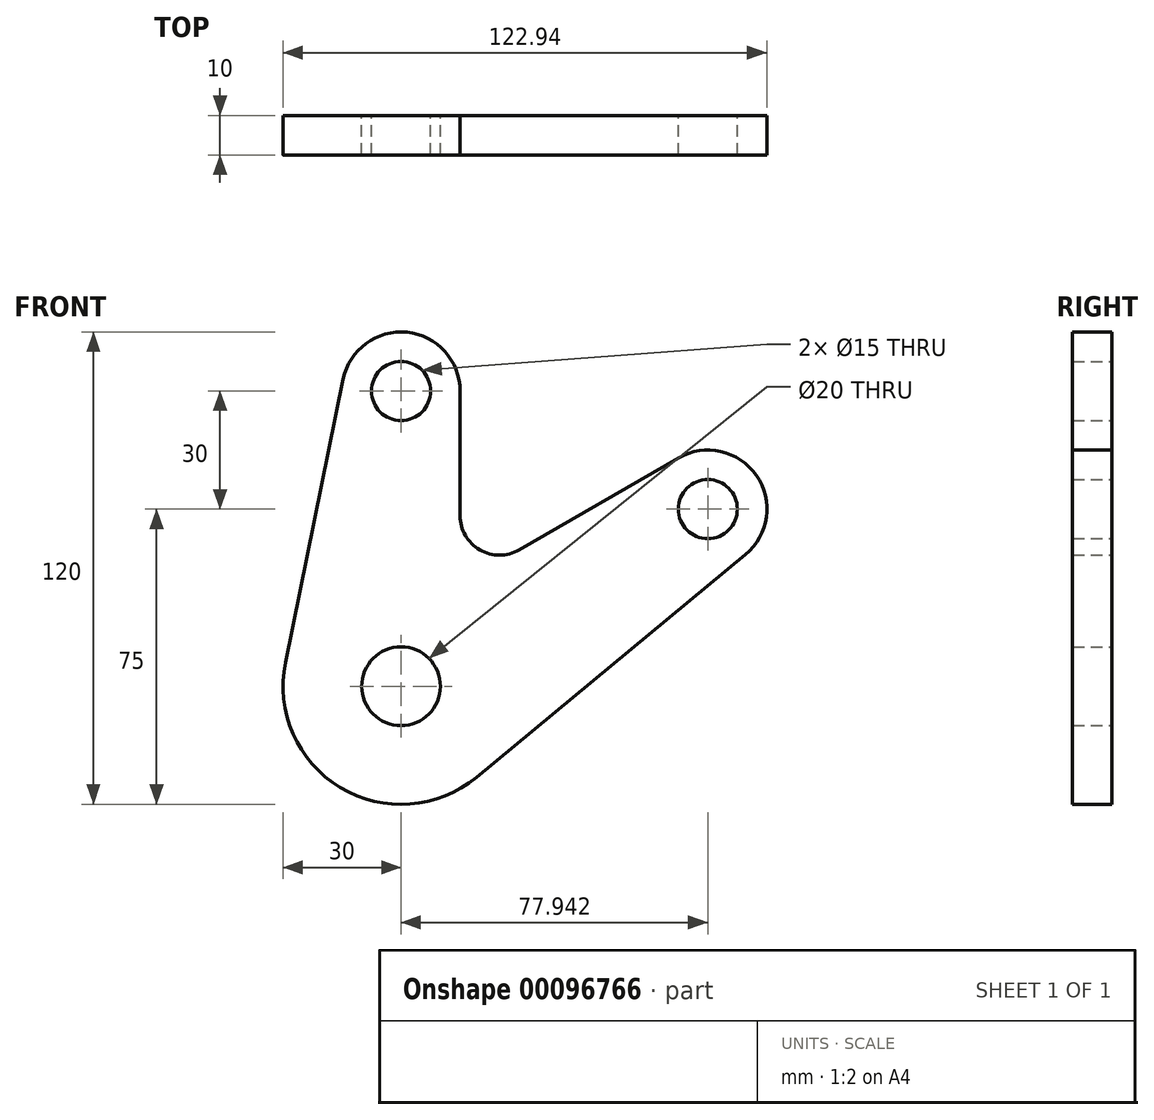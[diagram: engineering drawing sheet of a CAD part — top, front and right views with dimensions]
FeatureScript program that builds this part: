
annotation { "Feature Type Name" : "Feature", "Feature Type Description" : "" }
export const myFeature = defineFeature(function(context is Context, id is Id, definition is map)
    precondition{}
    {
        {
            var Q0;
            Q0=qCreatedBy(makeId("Front.planeOp"),FACE);
            var sketch = newSketch(context, id + "F0", { "sketchPlane" : qUnion([Q0])});
            skCircle(sketch, "E0", {"center": v(0, 0) * mm, "radius": 10 * mm});
            skCircle(sketch, "E1", {"center": v(0, 75) * mm, "radius": 7.5 * mm});
            skCircle(sketch, "E2", {"center": v(77.94, 45) * mm, "radius": 7.5 * mm});
            skLineSegment(sketch, "E3", {"start": v(0, 75) * mm, "end": v(0, 0) * mm, "construction": true});
            skLineSegment(sketch, "E4", {"start": v(0, 0) * mm, "end": v(77.94, 45) * mm, "construction": true});
            skArc(sketch, "E5", {"start": v(15, 75) * mm, "mid": v(1.5, 89.92) * mm, "end": v(-14.7, 78) * mm});
            skArc(sketch, "E6", {"start": v(87.5, 33.44) * mm, "mid": v(90.26, 53.56) * mm, "end": v(70.44, 58) * mm});
            skArc(sketch, "E7", {"start": v(-29.4, 6) * mm, "mid": v(-15.44, -25.72) * mm, "end": v(19.12, -23.12) * mm});
            skLineSegment(sketch, "E8", {"start": v(-14.7, 78) * mm, "end": v(-29.4, 6) * mm});
            skLineSegment(sketch, "E9", {"start": v(87.5, 33.44) * mm, "end": v(19.12, -23.12) * mm});
            skLineSegment(sketch, "E10", {"start": v(70.44, 58) * mm, "end": v(30, 34.64) * mm});
            skLineSegment(sketch, "E11", {"start": v(15, 75) * mm, "end": v(15, 43.3) * mm});
            skArc(sketch, "E12", {"start": v(15, 43.3) * mm, "mid": v(20, 34.64) * mm, "end": v(30, 34.64) * mm});
            skSolve(sketch);
        }
        {
            var Q0;
            Q0=makeQuery(id+"F0.imprint","IMPRINT",FACE,{"disambiguationData":[TD([[makeQuery(id+"F0.imprint","IMPRINT",EDGE,{"derivedFrom":sQuery(id+"F0.wireOp",EDGE,"E0")}),-1.0]])]});
            extrude(context, id + "F1", {"entities" : qUnion([Q0]), "depth" : 10 * mm});
        }
    });
